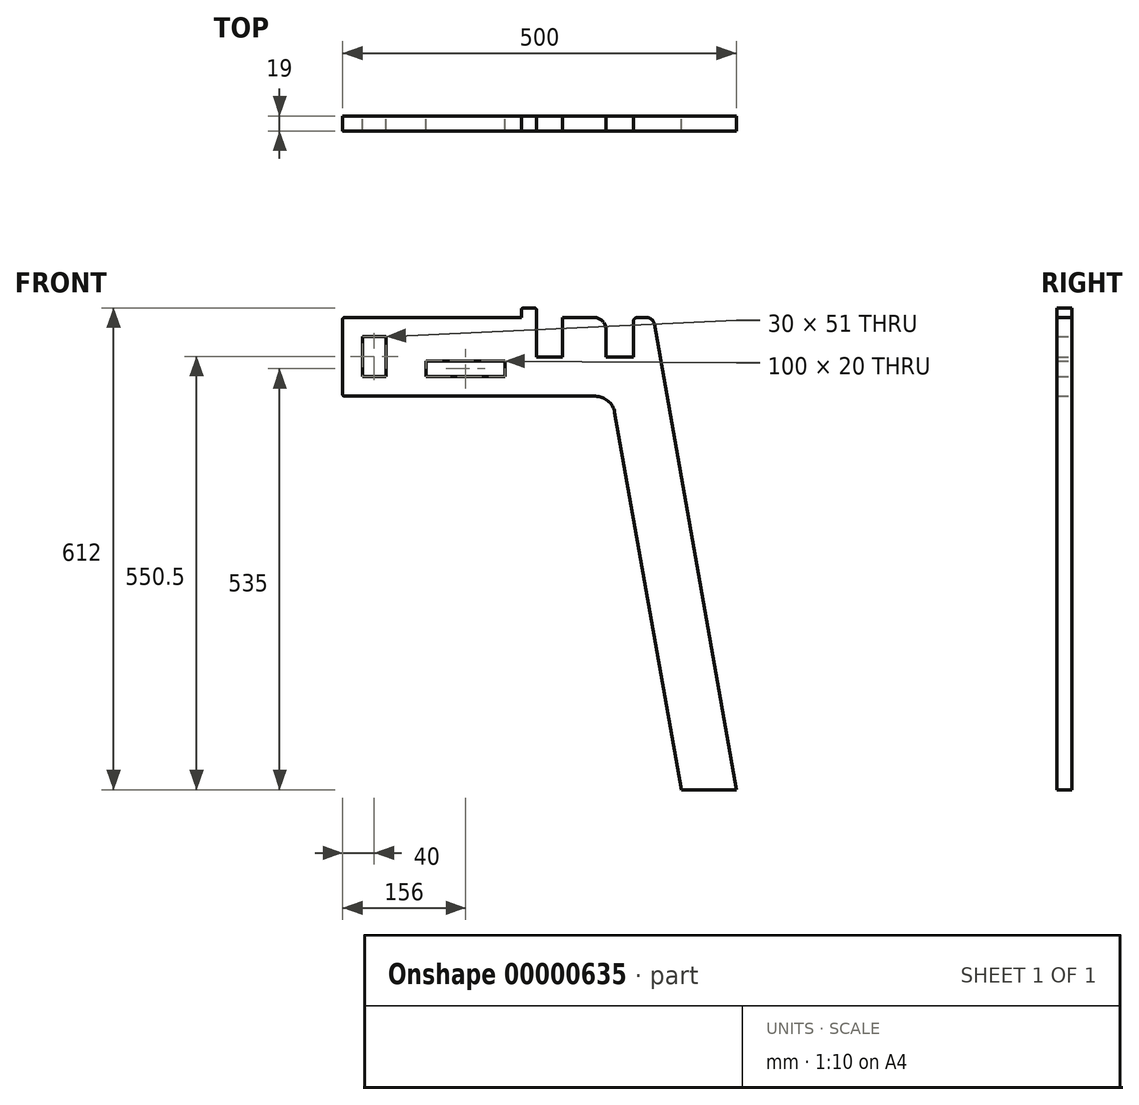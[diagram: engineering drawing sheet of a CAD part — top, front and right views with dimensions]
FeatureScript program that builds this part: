
annotation { "Feature Type Name" : "Feature", "Feature Type Description" : "" }
export const myFeature = defineFeature(function(context is Context, id is Id, definition is map)
    precondition{}
    {
        {
            var Q0;
            Q0=qCreatedBy(makeId("Front.planeOp"),FACE);
            var sketch = newSketch(context, id + "F0", { "sketchPlane" : qUnion([Q0])});
            skLineSegment(sketch, "E0", {"start": v(0, 2) * mm, "end": v(0, 98) * mm});
            skLineSegment(sketch, "E1", {"start": v(2, 100) * mm, "end": v(227, 100) * mm});
            skLineSegment(sketch, "E2", {"start": v(2, 0) * mm, "end": v(320.86, 0) * mm});
            skLineSegment(sketch, "E3", {"start": v(345.48, -20.66) * mm, "end": v(430, -500) * mm});
            skLineSegment(sketch, "E4", {"start": v(430, -500) * mm, "end": v(500, -500) * mm});
            skLineSegment(sketch, "E5", {"start": v(500, -500) * mm, "end": v(395.66, 91.74) * mm});
            skPoint(sketch, "E6.visualSharp", {"position": v(341.84, 0) * mm});
            skArc(sketch, "E6.filletArc", {"start": v(345.48, -20.66) * mm, "mid": v(336.93, -5.85) * mm, "end": v(320.86, 0) * mm});
            skLineSegment(sketch, "E7.bottom", {"start": v(25, 76) * mm, "end": v(55, 76) * mm});
            skLineSegment(sketch, "E7.top", {"start": v(25, 25) * mm, "end": v(55, 25) * mm});
            skLineSegment(sketch, "E7.left", {"start": v(25, 76) * mm, "end": v(25, 25) * mm});
            skLineSegment(sketch, "E7.right", {"start": v(55, 76) * mm, "end": v(55, 25) * mm});
            skLineSegment(sketch, "E8.top", {"start": v(246, 50) * mm, "end": v(279, 50) * mm});
            skLineSegment(sketch, "E8.left", {"start": v(246, 110) * mm, "end": v(246, 50) * mm});
            skLineSegment(sketch, "E8.right", {"start": v(279, 100) * mm, "end": v(279, 50) * mm});
            skLineSegment(sketch, "E9", {"start": v(244, 112) * mm, "end": v(229, 112) * mm});
            skLineSegment(sketch, "E10", {"start": v(227, 110) * mm, "end": v(227, 100) * mm});
            skLineSegment(sketch, "E11.trimOffspring", {"start": v(279, 100) * mm, "end": v(319.2, 100) * mm});
            skLineSegment(sketch, "E12.top", {"start": v(334.2, 50) * mm, "end": v(369.2, 50) * mm});
            skLineSegment(sketch, "E12.left", {"start": v(334.2, 85) * mm, "end": v(334.2, 50) * mm});
            skLineSegment(sketch, "E12.right", {"start": v(369.2, 95) * mm, "end": v(369.2, 50) * mm});
            skLineSegment(sketch, "E13.trimOffspring", {"start": v(374.2, 100) * mm, "end": v(385.81, 100) * mm});
            skPoint(sketch, "E14.visualSharp", {"position": v(334.2, 100) * mm});
            skArc(sketch, "E14.filletArc", {"start": v(334.2, 85) * mm, "mid": v(329.81, 95.6) * mm, "end": v(319.2, 100) * mm});
            skPoint(sketch, "E15.visualSharp", {"position": v(369.2, 100) * mm});
            skArc(sketch, "E15.filletArc", {"start": v(374.2, 100) * mm, "mid": v(370.67, 98.54) * mm, "end": v(369.2, 95) * mm});
            skPoint(sketch, "E16.visualSharp", {"position": v(394.2, 100) * mm});
            skArc(sketch, "E16.filletArc", {"start": v(395.66, 91.74) * mm, "mid": v(392.24, 97.66) * mm, "end": v(385.81, 100) * mm});
            skLineSegment(sketch, "E17.bottom", {"start": v(106, 45) * mm, "end": v(206, 45) * mm});
            skLineSegment(sketch, "E17.top", {"start": v(106, 25) * mm, "end": v(206, 25) * mm});
            skLineSegment(sketch, "E17.left", {"start": v(106, 45) * mm, "end": v(106, 25) * mm});
            skLineSegment(sketch, "E17.right", {"start": v(206, 45) * mm, "end": v(206, 25) * mm});
            skPoint(sketch, "E18.visualSharp", {"position": v(246, 112) * mm});
            skArc(sketch, "E18.filletArc", {"start": v(246, 110) * mm, "mid": v(245.41, 111.41) * mm, "end": v(244, 112) * mm});
            skPoint(sketch, "E19.visualSharp", {"position": v(227, 112) * mm});
            skArc(sketch, "E19.filletArc", {"start": v(229, 112) * mm, "mid": v(227.59, 111.41) * mm, "end": v(227, 110) * mm});
            skPoint(sketch, "E20.visualSharp", {"position": v(0, 100) * mm});
            skArc(sketch, "E20.filletArc", {"start": v(2, 100) * mm, "mid": v(0.59, 99.41) * mm, "end": v(0, 98) * mm});
            skPoint(sketch, "E21.visualSharp", {"position": v(0, 0) * mm});
            skArc(sketch, "E21.filletArc", {"start": v(0, 2) * mm, "mid": v(0.59, 0.59) * mm, "end": v(2, 0) * mm});
            skSolve(sketch);
        }
        {
            var Q0;
            Q0=makeQuery(id+"F0.imprint","IMPRINT",FACE,{"disambiguationData":[TD([[makeQuery(id+"F0.imprint","IMPRINT",EDGE,{"derivedFrom":sQuery(id+"F0.wireOp",EDGE,"E0")}),-1.0]])]});
            extrude(context, id + "F1", {"entities" : qUnion([Q0]), "depth" : 19 * mm});
        }
    });
